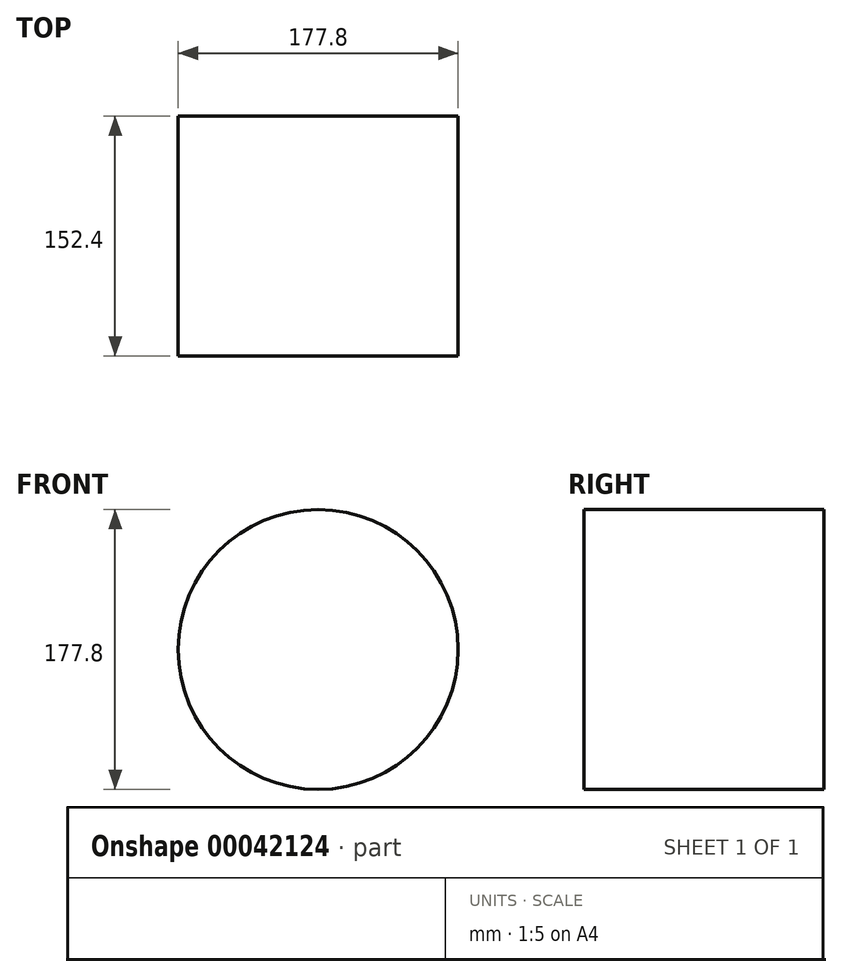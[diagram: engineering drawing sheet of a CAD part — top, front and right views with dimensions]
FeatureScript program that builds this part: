
annotation { "Feature Type Name" : "Feature", "Feature Type Description" : "" }
export const myFeature = defineFeature(function(context is Context, id is Id, definition is map)
    precondition{}
    {
        {
            var Q0;
            Q0=qCreatedBy(makeId("Front.planeOp"),FACE);
            var sketch = newSketch(context, id + "F0", { "sketchPlane" : qUnion([Q0])});
            skCircle(sketch, "E0", {"center": v(0, 0) * mm, "radius": 88.9 * mm});
            skSolve(sketch);
        }
        {
            var Q0;
            Q0 = qSketchRegion(id + "F0", true);
            extrude(context, id + "F1", {"entities" : qUnion([Q0]), "depth" : 152.4 * mm});
        }
    });
